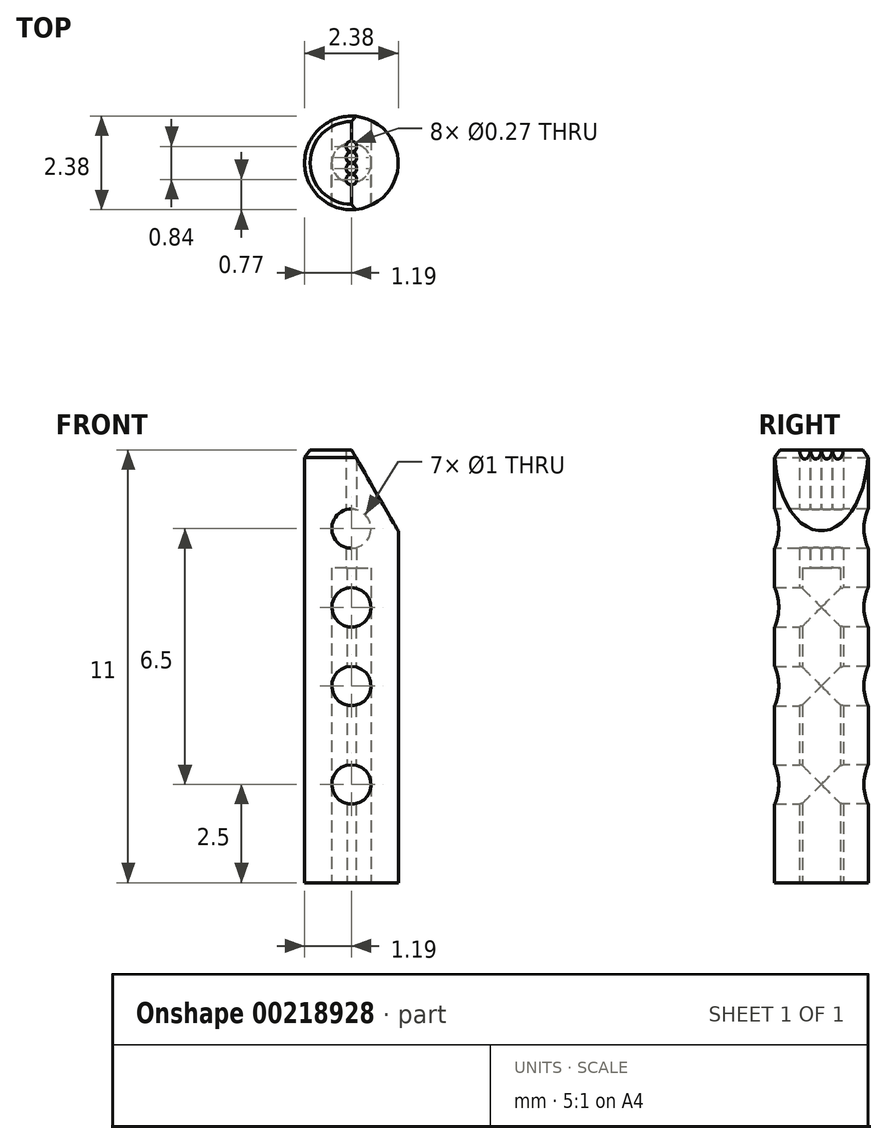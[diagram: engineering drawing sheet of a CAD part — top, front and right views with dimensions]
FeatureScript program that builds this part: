
annotation { "Feature Type Name" : "Feature", "Feature Type Description" : "" }
export const myFeature = defineFeature(function(context is Context, id is Id, definition is map)
    precondition{}
    {
        {
            var Q0;
            Q0=qCreatedBy(makeId("Right.planeOp"),FACE);
            var sketch = newSketch(context, id + "F0", { "sketchPlane" : qUnion([Q0])});
            skLineSegment(sketch, "E0", {"start": v(0, 0) * mm, "end": v(0, 11) * mm});
            skLineSegment(sketch, "E1", {"start": v(0, 11) * mm, "end": v(-1.05, 11) * mm});
            skLineSegment(sketch, "E2", {"start": v(-1.2, 10.8) * mm, "end": v(-1.19, 0) * mm});
            skLineSegment(sketch, "E3", {"start": v(-1.19, 0) * mm, "end": v(0, 0) * mm});
            skLineSegment(sketch, "E4", {"start": v(-1.05, 11) * mm, "end": v(-1.2, 10.8) * mm});
            skSolve(sketch);
        }
        {
            var Q0;
            Q0=makeQuery(id+"F0.imprint","IMPRINT",FACE,{"disambiguationData":[TD([[makeQuery(id+"F0.imprint","IMPRINT",EDGE,{"derivedFrom":sQuery(id+"F0.wireOp",EDGE,"E0")}),1.0]])]});
            var Q1;
            Q1=sQuery(id+"F0.wireOp",EDGE,"E0");
            revolve(context, id + "F1", {"entities" : qUnion([Q0]), "axis" : qUnion([Q1]), "revolveType" : RevolveType.FULL});
        }
        {
            var Q0;
            Q0=makeQuery(id+"F1.opRevolve","SWEPT_FACE",FACE,{"disambiguationData":[OSD([sQuery(id+"F0.wireOp",EDGE,"E3")])]});
            var sketch = newSketch(context, id + "F2", { "sketchPlane" : qUnion([Q0])});
            skCircle(sketch, "E5", {"center": v(0, 0) * mm, "radius": 0.5 * mm});
            skSolve(sketch);
        }
        {
            var Q0;
            Q0=qSketchRegion(id+"F2",true);
            extrude(context, id + "F3", {"entities" : qUnion([Q0]), "operationType" : NewBodyOperationType.REMOVE, "oppositeDirection" : true, "depth" : 8 * mm});
        }
        {
            var Q0;
            Q0=qCreatedBy(makeId("Front.planeOp"),FACE);
            var sketch = newSketch(context, id + "F4", { "sketchPlane" : qUnion([Q0])});
            skCircle(sketch, "E6", {"center": v(0, 20.84) * mm, "radius": 0.71 * mm});
            skCircle(sketch, "E7", {"center": v(0, 9) * mm, "radius": 0.5 * mm});
            skCircle(sketch, "E8", {"center": v(0, 7) * mm, "radius": 0.5 * mm});
            skCircle(sketch, "E9", {"center": v(0, 5) * mm, "radius": 0.5 * mm});
            skCircle(sketch, "E10", {"center": v(0, 2.5) * mm, "radius": 0.5 * mm});
            skCircle(sketch, "E11", {"center": v(0, 12) * mm, "radius": 0.5 * mm});
            skSolve(sketch);
        }
        {
            var Q0;
            Q0=qSketchRegion(id+"F4",true);
            extrude(context, id + "F5", {"entities" : qUnion([Q0]), "operationType" : NewBodyOperationType.REMOVE, "oppositeDirection" : true, "depth" : 25 * mm});
        }
        {
            var Q0;
            Q0=qSketchRegion(id+"F4",true);
            extrude(context, id + "F6", {"entities" : qUnion([Q0]), "operationType" : NewBodyOperationType.REMOVE, "depth" : 25 * mm});
        }
        {
            var Q0;
            Q0=qCreatedBy(makeId("Front.planeOp"),FACE);
            var sketch = newSketch(context, id + "F7", { "sketchPlane" : qUnion([Q0])});
            skLineSegment(sketch, "E12", {"start": v(0, 11) * mm, "end": v(1.58, 11) * mm});
            skLineSegment(sketch, "E13", {"start": v(1.58, 11) * mm, "end": v(1.58, 8.26) * mm});
            skLineSegment(sketch, "E14", {"start": v(1.58, 8.26) * mm, "end": v(0, 11) * mm});
            skSolve(sketch);
        }
        {
            var Q0;
            Q0=qSketchRegion(id+"F7",true);
            extrude(context, id + "F8", {"entities" : qUnion([Q0]), "operationType" : NewBodyOperationType.REMOVE, "oppositeDirection" : true, "depth" : 5 * mm});
        }
        {
            var Q0;
            Q0=qSketchRegion(id+"F7",true);
            extrude(context, id + "F9", {"entities" : qUnion([Q0]), "operationType" : NewBodyOperationType.REMOVE, "depth" : 25 * mm});
        }
        {
            var Q0;
            Q0=qCreatedBy(makeId("Top.planeOp"),FACE);
            var sketch = newSketch(context, id + "F10", { "sketchPlane" : qUnion([Q0])});
            skCircle(sketch, "E15", {"center": v(0, 0.42) * mm, "radius": 0.14 * mm});
            skCircle(sketch, "E16.0.1.0", {"center": v(0, 0.14) * mm, "radius": 0.14 * mm});
            skCircle(sketch, "E16.0.2.0", {"center": v(0, -0.14) * mm, "radius": 0.14 * mm});
            skCircle(sketch, "E16.0.3.0", {"center": v(0, -0.42) * mm, "radius": 0.14 * mm});
            skLineSegment(sketch, "E16.direction1", {"start": v(0, 0.42) * mm, "end": v(-0.02, 0.42) * mm, "construction": true});
            skLineSegment(sketch, "E16.direction2", {"start": v(0, 0.42) * mm, "end": v(0, 0.14) * mm, "construction": true});
            skSolve(sketch);
        }
        {
            var Q0;
            Q0 = qSketchRegion(id + "F10", true);
            extrude(context, id + "F11", {"entities" : qUnion([Q0]), "operationType" : NewBodyOperationType.REMOVE, "depth" : 25 * mm});
        }
    });
